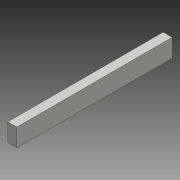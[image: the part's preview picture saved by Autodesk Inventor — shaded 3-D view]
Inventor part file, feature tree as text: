
AUTODESK INVENTOR PART (.ipt)
format: ipt  version: 2016 (Build 200138000, 138)  size: 69,120 bytes
history: native  units: mm
features: extrude x1, sketch x1
ambient origin geometry x8: Origin, YZ Plane, XZ Plane, XY Plane, X Axis, Y Axis, Z Axis, Center Point
bodies: 实体1 (feature_tree)
feature tree (2):
  extrude  "拉伸1"  Depth=20.0mm
  sketch  "草图1"  dims[d0=40.0mm d1=20.0mm d2=344.799mm d3=0.0mm]
